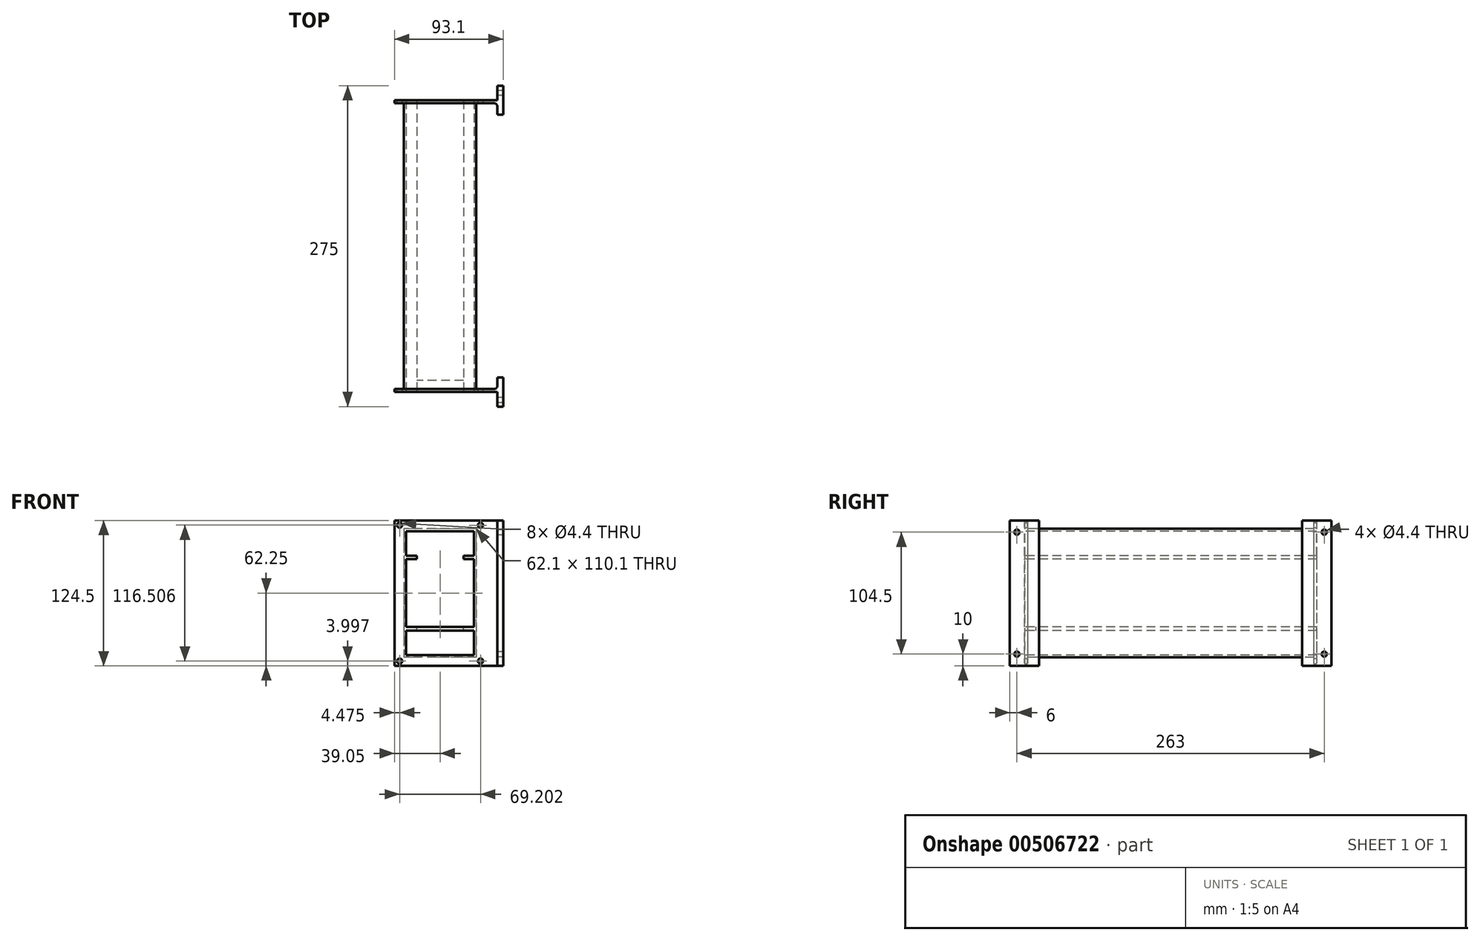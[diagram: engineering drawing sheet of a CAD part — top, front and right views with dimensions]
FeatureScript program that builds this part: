
annotation { "Feature Type Name" : "Feature", "Feature Type Description" : "" }
export const myFeature = defineFeature(function(context is Context, id is Id, definition is map)
    precondition{}
    {
        {
            var Q0;
            Q0=qCreatedBy(makeId("Front.planeOp"),FACE);
            var sketch = newSketch(context, id + "F0", { "sketchPlane" : qUnion([Q0])});
            skLineSegment(sketch, "E0.bottom", {"start": v(39.05, 62.25) * mm, "end": v(-39.05, 62.25) * mm});
            skLineSegment(sketch, "E0.top", {"start": v(39.05, -62.25) * mm, "end": v(-39.05, -62.25) * mm});
            skLineSegment(sketch, "E0.left", {"start": v(39.05, 62.25) * mm, "end": v(39.05, -62.25) * mm});
            skLineSegment(sketch, "E0.right", {"start": v(-39.05, 62.25) * mm, "end": v(-39.05, -62.25) * mm});
            skPoint(sketch, "E0.middle", {"position": v(0, 0) * mm});
            skLineSegment(sketch, "E1.bottom", {"start": v(29.05, 29.05) * mm, "end": v(-29.05, 29.05) * mm});
            skLineSegment(sketch, "E1.top", {"start": v(29.05, -29.05) * mm, "end": v(-29.05, -29.05) * mm});
            skLineSegment(sketch, "E1.left", {"start": v(29.05, 29.05) * mm, "end": v(29.05, -29.05) * mm});
            skLineSegment(sketch, "E1.right", {"start": v(-29.05, 29.05) * mm, "end": v(-29.05, -29.05) * mm});
            skLineSegment(sketch, "E2.bottom", {"start": v(-29.05, 29.05) * mm, "end": v(29.05, 29.05) * mm});
            skLineSegment(sketch, "E2.top", {"start": v(-29.05, 53.05) * mm, "end": v(29.05, 53.05) * mm});
            skLineSegment(sketch, "E2.left", {"start": v(-29.05, 29.05) * mm, "end": v(-29.05, 53.05) * mm});
            skLineSegment(sketch, "E2.right", {"start": v(29.05, 29.05) * mm, "end": v(29.05, 53.05) * mm});
            skLineSegment(sketch, "E3.bottom", {"start": v(-29.05, -29.05) * mm, "end": v(29.05, -29.05) * mm});
            skLineSegment(sketch, "E3.top", {"start": v(-29.05, -53.05) * mm, "end": v(29.05, -53.05) * mm});
            skLineSegment(sketch, "E3.left", {"start": v(-29.05, -29.05) * mm, "end": v(-29.05, -53.05) * mm});
            skLineSegment(sketch, "E3.right", {"start": v(29.05, -29.05) * mm, "end": v(29.05, -53.05) * mm});
            skLineSegment(sketch, "E4", {"start": v(0, 33.08) * mm, "end": v(0, 29.05) * mm, "construction": true});
            skLineSegment(sketch, "E5", {"start": v(29.05, 0) * mm, "end": v(-29.05, 0) * mm, "construction": true});
            skLineSegment(sketch, "E6.0", {"start": v(-29.05, 32.05) * mm, "end": v(29.05, 32.05) * mm});
            skLineSegment(sketch, "E7.0", {"start": v(-20, 33.08) * mm, "end": v(-20, 29.05) * mm, "construction": true});
            skLineSegment(sketch, "E8.0", {"start": v(20, 33.08) * mm, "end": v(20, 29.05) * mm, "construction": true});
            skLineSegment(sketch, "E9.bottom", {"start": v(20, 32.05) * mm, "end": v(-20, 32.05) * mm});
            skLineSegment(sketch, "E9.top", {"start": v(20, 29.05) * mm, "end": v(-20, 29.05) * mm});
            skLineSegment(sketch, "E9.left", {"start": v(20, 32.05) * mm, "end": v(20, 29.05) * mm});
            skLineSegment(sketch, "E9.right", {"start": v(-20, 32.05) * mm, "end": v(-20, 29.05) * mm});
            skLineSegment(sketch, "E10.MirrorCS", {"start": v(20, -32.05) * mm, "end": v(20, -29.05) * mm});
            skLineSegment(sketch, "E11.MirrorCS", {"start": v(-29.05, -32.05) * mm, "end": v(29.05, -32.05) * mm});
            skLineSegment(sketch, "E12.MirrorCS", {"start": v(-20, -32.05) * mm, "end": v(-20, -29.05) * mm});
            skLineSegment(sketch, "E13.bottom", {"start": v(39.05, 62.25) * mm, "end": v(49.05, 62.25) * mm});
            skLineSegment(sketch, "E13.top", {"start": v(39.05, -62.25) * mm, "end": v(49.05, -62.25) * mm});
            skLineSegment(sketch, "E13.right", {"start": v(49.05, 62.25) * mm, "end": v(49.05, -62.25) * mm});
            skLineSegment(sketch, "E14.bottom", {"start": v(49.05, 62.25) * mm, "end": v(54.05, 62.25) * mm});
            skLineSegment(sketch, "E14.top", {"start": v(49.05, -62.25) * mm, "end": v(54.05, -62.25) * mm});
            skLineSegment(sketch, "E14.right", {"start": v(54.05, 62.25) * mm, "end": v(54.05, -62.25) * mm});
            skSolve(sketch);
        }
        {
            var Q0;
            Q0=makeQuery(id+"F0.imprint","IMPRINT",FACE,{"disambiguationData":[TD([[makeQuery(id+"F0.imprint","IMPRINT",EDGE,{"derivedFrom":sQuery(id+"F0.wireOp",EDGE,"E0.bottom")}),1.0]])]});
            extrude(context, id + "F1", {"entities" : qUnion([Q0]), "oppositeDirection" : true, "depth" : 2.5 * mm, "offsetDistance" : 25 * mm});
        }
        {
            var Q0;
            {var subQ3=sQuery(id+"F0.wireOp",EDGE,"E9.left");Q0=makeQuery(id+"F0.imprint","IMPRINT",FACE,{"disambiguationData":[TD([[makeQuery(id+"F0.imprint","IMPRINT",EDGE,{"derivedFrom":subQ3}),1.0]])]});}
            var Q1;
            {var subQ3=sQuery(id+"F0.wireOp",EDGE,"E9.right");Q1=makeQuery(id+"F0.imprint","IMPRINT",FACE,{"disambiguationData":[TD([[makeQuery(id+"F0.imprint","IMPRINT",EDGE,{"derivedFrom":subQ3}),-1.0]])]});}
            var Q2;
            {var subQ3=sQuery(id+"F0.wireOp",EDGE,"E10.MirrorCS");Q2=makeQuery(id+"F0.imprint","IMPRINT",FACE,{"disambiguationData":[TD([[makeQuery(id+"F0.imprint","IMPRINT",EDGE,{"derivedFrom":subQ3}),-1.0]])]});}
            var Q3;
            {var subQ3=sQuery(id+"F0.wireOp",EDGE,"E12.MirrorCS");Q3=makeQuery(id+"F0.imprint","IMPRINT",FACE,{"disambiguationData":[TD([[makeQuery(id+"F0.imprint","IMPRINT",EDGE,{"derivedFrom":subQ3}),1.0]])]});}
            extrude(context, id + "F2", {"entities" : qUnion([Q0, Q1, Q2, Q3]), "operationType" : NewBodyOperationType.ADD, "oppositeDirection" : true, "depth" : 250 * mm, "offsetDistance" : 25 * mm});
        }
        {
            var Q0;
            Q0=makeQuery(id+"F0.imprint","IMPRINT",FACE,{"disambiguationData":[TD([[makeQuery(id+"F0.imprint","IMPRINT",EDGE,{"derivedFrom":sQuery(id+"F0.wireOp",EDGE,"E9.bottom")}),1.0]])]});
            var Q1;
            {var subQ0=sQuery(id+"F0.wireOp",EDGE,"E10.MirrorCS");Q1=makeQuery(id+"F0.imprint","IMPRINT",FACE,{"disambiguationData":[TD([[makeQuery(id+"F0.imprint","IMPRINT",EDGE,{"derivedFrom":subQ0}),1.0]])]});}
            extrude(context, id + "F3", {"entities" : qUnion([Q0, Q1]), "operationType" : NewBodyOperationType.ADD, "oppositeDirection" : true, "depth" : 10 * mm, "offsetDistance" : 25 * mm});
        }
        {
            var Q0;
            Q0=makeQuery(id+"F1.opExtrude","CAP_FACE",FACE,{"disambiguationData":[OSD([sQuery(id+"F0.wireOp",EDGE,"E0.bottom"),sQuery(id+"F0.wireOp",EDGE,"E0.top"),sQuery(id+"F0.wireOp",EDGE,"E0.left"),sQuery(id+"F0.wireOp",EDGE,"E0.right"),sQuery(id+"F0.wireOp",EDGE,"E1.left"),sQuery(id+"F0.wireOp",EDGE,"E1.right"),sQuery(id+"F0.wireOp",EDGE,"E2.top"),sQuery(id+"F0.wireOp",EDGE,"E2.left"),sQuery(id+"F0.wireOp",EDGE,"E2.right"),sQuery(id+"F0.wireOp",EDGE,"E3.top"),sQuery(id+"F0.wireOp",EDGE,"E3.left"),sQuery(id+"F0.wireOp",EDGE,"E3.right"),sQuery(id+"F0.wireOp",EDGE,"4e601988-f2da-406f-8835-c61af852b349.0"),sQuery(id+"F0.wireOp",EDGE,"4e601988-f2da-406f-8835-c61af852b349.1"),sQuery(id+"F0.wireOp",EDGE,"4e601988-f2da-406f-8835-c61af852b349.2"),sQuery(id+"F0.wireOp",EDGE,"4e601988-f2da-406f-8835-c61af852b349.3")])],"isStart":false});
            cPlane(context, id + "F4", {"entities" : qUnion([Q0]), "cplaneType" : CPlaneType.OFFSET, "offset" : 0 * mm, "width" : 150 * mm, "height" : 150 * mm});
        }
        {
            var Q0;
            Q0=qCreatedBy(id+"F4.planeOp",FACE);
            var sketch = newSketch(context, id + "F5", { "sketchPlane" : qUnion([Q0])});
            skLineSegment(sketch, "E15.0", {"start": v(-29.05, -29.05) * mm, "end": v(-29.05, -53.05) * mm});
            skLineSegment(sketch, "E16.0", {"start": v(29.05, -29.05) * mm, "end": v(29.05, -53.05) * mm});
            skLineSegment(sketch, "E17.0", {"start": v(-29.05, 29.05) * mm, "end": v(-29.05, 53.05) * mm});
            skLineSegment(sketch, "E17.1", {"start": v(29.05, 29.05) * mm, "end": v(29.05, 53.05) * mm});
            skLineSegment(sketch, "E18.bottom", {"start": v(-29.05, 53.05) * mm, "end": v(29.05, 53.05) * mm});
            skLineSegment(sketch, "E18.top", {"start": v(-29.05, -53.05) * mm, "end": v(29.05, -53.05) * mm});
            skLineSegment(sketch, "E18.left", {"start": v(-29.05, 53.05) * mm, "end": v(-29.05, -53.05) * mm});
            skLineSegment(sketch, "E18.right", {"start": v(29.05, 53.05) * mm, "end": v(29.05, -53.05) * mm});
            skLineSegment(sketch, "E19.0", {"start": v(-31.05, 55.05) * mm, "end": v(31.05, 55.05) * mm});
            skLineSegment(sketch, "E19.1", {"start": v(-31.05, 55.05) * mm, "end": v(-31.05, -55.05) * mm});
            skLineSegment(sketch, "E19.2", {"start": v(-31.05, -55.05) * mm, "end": v(31.05, -55.05) * mm});
            skLineSegment(sketch, "E19.3", {"start": v(31.05, 55.05) * mm, "end": v(31.05, -55.05) * mm});
            skSolve(sketch);
        }
        {
            var Q0;
            {var subQ4=sQuery(id+"F5.wireOp",EDGE,"E18.bottom");Q0=makeQuery(id+"F5.imprint","IMPRINT",FACE,{"disambiguationData":[TD([[makeQuery(id+"F5.imprint","IMPRINT",EDGE,{"derivedFrom":subQ4}),1.0]])]});}
            extrude(context, id + "F6", {"entities" : qUnion([Q0]), "operationType" : NewBodyOperationType.ADD, "depth" : 247.5 * mm, "offsetDistance" : 25 * mm});
        }
        {
            var Q0;
            {var subQ0=sQuery(id+"F0.wireOp",EDGE,"E11.MirrorCS");var subQ1=sQuery(id+"F0.wireOp",EDGE,"E3.bottom");var subQ2=sQuery(id+"F0.wireOp",EDGE,"E6.0");var subQ3=sQuery(id+"F0.wireOp",EDGE,"E2.bottom");Q0=makeQuery(id+"F6.boolean.opBoolean","MERGE",FACE,{"derivedFrom":[makeQuery(id+"F2.opExtrude","CAP_FACE",FACE,{"disambiguationData":[OSD([subQ3,sQuery(id+"F0.wireOp",EDGE,"E2.left"),subQ2,sQuery(id+"F0.wireOp",EDGE,"E9.right")])],"isStart":false}),makeQuery(id+"F2.opExtrude","CAP_FACE",FACE,{"disambiguationData":[OSD([subQ3,sQuery(id+"F0.wireOp",EDGE,"E2.right"),subQ2,sQuery(id+"F0.wireOp",EDGE,"E9.left")])],"isStart":false}),makeQuery(id+"F2.opExtrude","CAP_FACE",FACE,{"disambiguationData":[OSD([subQ1,sQuery(id+"F0.wireOp",EDGE,"E3.left"),subQ0,sQuery(id+"F0.wireOp",EDGE,"E12.MirrorCS")])],"isStart":false}),makeQuery(id+"F2.opExtrude","CAP_FACE",FACE,{"disambiguationData":[OSD([subQ1,sQuery(id+"F0.wireOp",EDGE,"E3.right"),sQuery(id+"F0.wireOp",EDGE,"E10.MirrorCS"),subQ0])],"isStart":false}),makeQuery(id+"F6.opExtrude","CAP_FACE",FACE,{"disambiguationData":[OSD([sQuery(id+"F5.wireOp",EDGE,"E18.bottom"),sQuery(id+"F5.wireOp",EDGE,"E18.top"),sQuery(id+"F5.wireOp",EDGE,"E18.left"),sQuery(id+"F5.wireOp",EDGE,"E18.right"),sQuery(id+"F5.wireOp",EDGE,"E19.0"),sQuery(id+"F5.wireOp",EDGE,"E19.1"),sQuery(id+"F5.wireOp",EDGE,"E19.2"),sQuery(id+"F5.wireOp",EDGE,"E19.3")])],"isStart":false})]});}
            cPlane(context, id + "F7", {"entities" : qUnion([Q0]), "cplaneType" : CPlaneType.OFFSET, "offset" : 0 * mm, "width" : 150 * mm, "height" : 150 * mm});
        }
        {
            var Q0;
            Q0=qCreatedBy(id+"F7.planeOp",FACE);
            var sketch = newSketch(context, id + "F8", { "sketchPlane" : qUnion([Q0])});
            skLineSegment(sketch, "E20.2", {"start": v(39.05, 62.25) * mm, "end": v(39.05, -62.25) * mm});
            skLineSegment(sketch, "E20.4", {"start": v(-31.05, -55.05) * mm, "end": v(31.05, -55.05) * mm});
            skLineSegment(sketch, "E20.5", {"start": v(31.05, 55.05) * mm, "end": v(31.05, -55.05) * mm});
            skLineSegment(sketch, "E20.6", {"start": v(-31.05, 55.05) * mm, "end": v(-31.05, -55.05) * mm});
            skLineSegment(sketch, "E20.7", {"start": v(-31.05, 55.05) * mm, "end": v(31.05, 55.05) * mm});
            skLineSegment(sketch, "E20.8", {"start": v(-20, 32.05) * mm, "end": v(-29.05, 32.05) * mm});
            skLineSegment(sketch, "E20.9", {"start": v(-20, 32.05) * mm, "end": v(-20, 29.05) * mm});
            skLineSegment(sketch, "E20.10", {"start": v(-20, 29.05) * mm, "end": v(-29.05, 29.05) * mm});
            skLineSegment(sketch, "E20.11", {"start": v(-20, 32.05) * mm, "end": v(20, 32.05) * mm});
            skLineSegment(sketch, "E20.12", {"start": v(-20, 29.05) * mm, "end": v(20, 29.05) * mm});
            skLineSegment(sketch, "E20.13", {"start": v(-29.05, 29.05) * mm, "end": v(-29.05, -29.05) * mm});
            skLineSegment(sketch, "E20.14", {"start": v(20, 32.05) * mm, "end": v(20, 29.05) * mm});
            skLineSegment(sketch, "E20.15", {"start": v(29.05, 32.05) * mm, "end": v(20, 32.05) * mm});
            skLineSegment(sketch, "E20.16", {"start": v(29.05, 29.05) * mm, "end": v(20, 29.05) * mm});
            skLineSegment(sketch, "E20.17", {"start": v(29.05, 29.05) * mm, "end": v(29.05, -29.05) * mm});
            skLineSegment(sketch, "E20.18", {"start": v(-20, -29.05) * mm, "end": v(-29.05, -29.05) * mm});
            skLineSegment(sketch, "E20.19", {"start": v(20, -32.05) * mm, "end": v(-20, -32.05) * mm});
            skLineSegment(sketch, "E20.20", {"start": v(20, -29.05) * mm, "end": v(-20, -29.05) * mm});
            skLineSegment(sketch, "E20.21", {"start": v(-20, -32.05) * mm, "end": v(-29.05, -32.05) * mm});
            skLineSegment(sketch, "E20.22", {"start": v(-20, -32.05) * mm, "end": v(-20, -29.05) * mm});
            skLineSegment(sketch, "E20.23", {"start": v(20, -32.05) * mm, "end": v(20, -29.05) * mm});
            skLineSegment(sketch, "E20.24", {"start": v(29.05, -32.05) * mm, "end": v(20, -32.05) * mm});
            skLineSegment(sketch, "E20.25", {"start": v(29.05, -29.05) * mm, "end": v(20, -29.05) * mm});
            skLineSegment(sketch, "E20.26", {"start": v(-29.05, -32.05) * mm, "end": v(-29.05, -53.05) * mm});
            skLineSegment(sketch, "E20.27", {"start": v(-29.05, -53.05) * mm, "end": v(29.05, -53.05) * mm});
            skLineSegment(sketch, "E20.28", {"start": v(29.05, -32.05) * mm, "end": v(29.05, -53.05) * mm});
            skLineSegment(sketch, "E20.29", {"start": v(-29.05, 53.05) * mm, "end": v(-29.05, 32.05) * mm});
            skLineSegment(sketch, "E20.30", {"start": v(-29.05, 53.05) * mm, "end": v(29.05, 53.05) * mm});
            skLineSegment(sketch, "E20.31", {"start": v(29.05, 53.05) * mm, "end": v(29.05, 32.05) * mm});
            skLineSegment(sketch, "E21.0", {"start": v(-49.05, 62.25) * mm, "end": v(-49.05, -62.25) * mm});
            skLineSegment(sketch, "E22.bottom", {"start": v(-49.05, 62.25) * mm, "end": v(39.05, 62.25) * mm});
            skLineSegment(sketch, "E22.top", {"start": v(-49.05, -62.25) * mm, "end": v(39.05, -62.25) * mm});
            skLineSegment(sketch, "E23.0", {"start": v(-39.05, 62.25) * mm, "end": v(-39.05, -62.25) * mm});
            skLineSegment(sketch, "E24", {"start": v(-39.05, -62.25) * mm, "end": v(-34.63, -58.2) * mm, "construction": true});
            skLineSegment(sketch, "E25", {"start": v(39.05, -62.25) * mm, "end": v(34.58, -58.25) * mm, "construction": true});
            skLineSegment(sketch, "E26.MirrorCS", {"start": v(-39.05, 62.25) * mm, "end": v(-34.63, 58.2) * mm, "construction": true});
            skLineSegment(sketch, "E27.MirrorCS", {"start": v(39.05, 62.25) * mm, "end": v(34.58, 58.25) * mm, "construction": true});
            skLineSegment(sketch, "E28.0.0", {"start": v(-54.05, 62.25) * mm, "end": v(-49.05, 62.25) * mm});
            skLineSegment(sketch, "E28.0.2", {"start": v(-49.05, -62.25) * mm, "end": v(-54.05, -62.25) * mm});
            skLineSegment(sketch, "E28.0.3", {"start": v(-54.05, -62.25) * mm, "end": v(-54.05, 62.25) * mm});
            skSolve(sketch);
        }
        {
            var Q0;
            Q0=makeQuery(id+"F8.imprint","IMPRINT",FACE,{"disambiguationData":[TD([[makeQuery(id+"F8.imprint","IMPRINT",EDGE,{"derivedFrom":sQuery(id+"F8.wireOp",EDGE,"E20.4")}),-1.0]])]});
            extrude(context, id + "F9", {"entities" : qUnion([Q0]), "operationType" : NewBodyOperationType.ADD, "oppositeDirection" : true, "depth" : 2.5 * mm, "offsetDistance" : 25 * mm});
        }
        {
            var Q0;
            Q0=makeQuery(id+"F8.imprint","IMPRINT",FACE,{"disambiguationData":[TD([[makeQuery(id+"F8.imprint","IMPRINT",EDGE,{"derivedFrom":sQuery(id+"F8.wireOp",EDGE,"E28.0.0")}),-1.0]])]});
            extrude(context, id + "F10", {"entities" : qUnion([Q0]), "operationType" : NewBodyOperationType.ADD, "depth" : 12.5 * mm, "offsetDistance" : 25 * mm, "hasSecondDirection" : true, "secondDirectionOppositeDirection" : true, "secondDirectionDepth" : 12.5 * mm});
        }
        {
            var Q0;
            Q0=makeQuery(id+"F0.imprint","IMPRINT",FACE,{"disambiguationData":[TD([[makeQuery(id+"F0.imprint","IMPRINT",EDGE,{"derivedFrom":sQuery(id+"F0.wireOp",EDGE,"E14.bottom")}),-1.0]])]});
            extrude(context, id + "F11", {"entities" : qUnion([Q0]), "operationType" : NewBodyOperationType.ADD, "depth" : 12.5 * mm, "offsetDistance" : 25 * mm, "hasSecondDirection" : true, "secondDirectionOppositeDirection" : true, "secondDirectionDepth" : 12.5 * mm});
        }
        {
            var Q0;
            Q0=makeQuery(id+"F11.opExtrude","SWEPT_FACE",FACE,{"disambiguationData":[OSD([sQuery(id+"F0.wireOp",EDGE,"E14.right")])]});
            cPlane(context, id + "F12", {"entities" : qUnion([Q0]), "cplaneType" : CPlaneType.OFFSET, "offset" : 0 * mm, "width" : 150 * mm, "height" : 150 * mm});
        }
        {
            var Q0;
            Q0=qCreatedBy(id+"F12.planeOp",FACE);
            var sketch = newSketch(context, id + "F13", { "sketchPlane" : qUnion([Q0])});
            skLineSegment(sketch, "E29.0.0", {"start": v(12.5, -62.25) * mm, "end": v(12.5, 62.25) * mm});
            skLineSegment(sketch, "E29.0.1", {"start": v(12.5, 62.25) * mm, "end": v(-12.5, 62.25) * mm});
            skLineSegment(sketch, "E29.0.2", {"start": v(-12.5, 62.25) * mm, "end": v(-12.5, -62.25) * mm});
            skLineSegment(sketch, "E29.0.3", {"start": v(-12.5, -62.25) * mm, "end": v(12.5, -62.25) * mm});
            skLineSegment(sketch, "E30", {"start": v(-12.5, 62.25) * mm, "end": v(-6.5, 62.25) * mm, "construction": true});
            skLineSegment(sketch, "E31", {"start": v(-6.5, 62.25) * mm, "end": v(-6.5, 52.25) * mm, "construction": true});
            skLineSegment(sketch, "E32", {"start": v(-12.5, 0) * mm, "end": v(0, 0) * mm, "construction": true});
            skLineSegment(sketch, "E33.MirrorCS", {"start": v(-6.5, -62.25) * mm, "end": v(-6.5, -52.25) * mm, "construction": true});
            skLineSegment(sketch, "E34.MirrorCS", {"start": v(-12.5, -62.25) * mm, "end": v(-6.5, -62.25) * mm, "construction": true});
            skLineSegment(sketch, "E35", {"start": v(-12.5, 0) * mm, "end": v(-8.96, 0) * mm, "construction": true});
            skSolve(sketch);
        }
        {
            var Q0;
            Q0=makeQuery(id+"F10.opExtrude","SWEPT_FACE",FACE,{"disambiguationData":[OSD([sQuery(id+"F8.wireOp",EDGE,"E28.0.3")])]});
            cPlane(context, id + "F14", {"entities" : qUnion([Q0]), "cplaneType" : CPlaneType.OFFSET, "offset" : 0 * mm, "width" : 150 * mm, "height" : 150 * mm});
        }
        {
            var Q0;
            Q0=qCreatedBy(id+"F14.planeOp",FACE);
            var sketch = newSketch(context, id + "F15", { "sketchPlane" : qUnion([Q0])});
            skLineSegment(sketch, "E36.0.0", {"start": v(237.5, 62.25) * mm, "end": v(237.5, -62.25) * mm});
            skLineSegment(sketch, "E36.0.1", {"start": v(237.5, -62.25) * mm, "end": v(262.5, -62.25) * mm});
            skLineSegment(sketch, "E36.0.2", {"start": v(262.5, -62.25) * mm, "end": v(262.5, 62.25) * mm});
            skLineSegment(sketch, "E36.0.3", {"start": v(262.5, 62.25) * mm, "end": v(237.5, 62.25) * mm});
            skLineSegment(sketch, "E37", {"start": v(262.5, 62.25) * mm, "end": v(256.5, 62.25) * mm, "construction": true});
            skLineSegment(sketch, "E38", {"start": v(256.5, 62.25) * mm, "end": v(256.5, 52.25) * mm, "construction": true});
            skLineSegment(sketch, "E39", {"start": v(262.5, 0) * mm, "end": v(237.5, 0) * mm, "construction": true});
            skLineSegment(sketch, "E40.MirrorCS", {"start": v(262.5, -62.25) * mm, "end": v(256.5, -62.25) * mm, "construction": true});
            skLineSegment(sketch, "E41.MirrorCS", {"start": v(262.5, 62.25) * mm, "end": v(262.5, -62.25) * mm});
            skLineSegment(sketch, "E42.MirrorCS", {"start": v(262.5, -62.25) * mm, "end": v(237.5, -62.25) * mm});
            skLineSegment(sketch, "E43.MirrorCS", {"start": v(256.5, -62.25) * mm, "end": v(256.5, -52.25) * mm, "construction": true});
            skSolve(sketch);
        }
        {
            var Q0;
            Q0=sQuery(id+"F8.wireOp",VERTEX,"E26.MirrorCS.end");
            var Q1;
            Q1=sQuery(id+"F8.wireOp",VERTEX,"E27.MirrorCS.end");
            var Q2;
            Q2=sQuery(id+"F8.wireOp",VERTEX,"E24.end");
            var Q3;
            Q3=sQuery(id+"F8.wireOp",VERTEX,"E25.end");
            var Q4;
            Q4=makeQuery(id+"F1.opExtrude","SWEPT_BODY",BODY,{"disambiguationData":[OSD([sQuery(id+"F0.wireOp",EDGE,"E0.bottom"),sQuery(id+"F0.wireOp",EDGE,"E0.top"),sQuery(id+"F0.wireOp",EDGE,"E0.right"),sQuery(id+"F0.wireOp",EDGE,"E1.left"),sQuery(id+"F0.wireOp",EDGE,"E1.right"),sQuery(id+"F0.wireOp",EDGE,"E2.top"),sQuery(id+"F0.wireOp",EDGE,"E2.left"),sQuery(id+"F0.wireOp",EDGE,"E2.right"),sQuery(id+"F0.wireOp",EDGE,"E3.top"),sQuery(id+"F0.wireOp",EDGE,"E3.left"),sQuery(id+"F0.wireOp",EDGE,"E3.right"),sQuery(id+"F0.wireOp",EDGE,"4e601988-f2da-406f-8835-c61af852b349.0"),sQuery(id+"F0.wireOp",EDGE,"4e601988-f2da-406f-8835-c61af852b349.1"),sQuery(id+"F0.wireOp",EDGE,"4e601988-f2da-406f-8835-c61af852b349.2"),sQuery(id+"F0.wireOp",EDGE,"4e601988-f2da-406f-8835-c61af852b349.3"),sQuery(id+"F0.wireOp",EDGE,"E0.left")])]});
            hole(context, id + "F16", {"style" : HoleStyle.SIMPLE, "endStyle" : HoleEndStyle.THROUGH, "standardTappedOrClearance" : lookupTablePath({ "standard" : "ISO", "fit" : "Normal", "size" : "M4", "type" : "Clearance" }), "standardBlindInLast" : lookupTablePath({ "fit" : "Standard", "standard" : "ISO", "size" : "M4", "type" : "Clearance" }), "holeDiameter" : 4.4 * mm, "majorDiameter" : 5 * mm, "isTappedThrough" : true, "tappedDepth" : 12 * mm, "tapClearance" : 3, "locations" : qUnion([Q0, Q1, Q2, Q3]), "scope" : qUnion([Q4])});
        }
        {
            var Q0;
            Q0=makeQuery(id+"F0.imprint","IMPRINT",FACE,{"disambiguationData":[TD([[makeQuery(id+"F0.imprint","IMPRINT",EDGE,{"derivedFrom":sQuery(id+"F0.wireOp",EDGE,"E13.bottom")}),-1.0]])]});
            extrude(context, id + "F17", {"entities" : qUnion([Q0]), "operationType" : NewBodyOperationType.ADD, "oppositeDirection" : true, "depth" : 2.5 * mm, "offsetDistance" : 25 * mm});
        }
        {
            var Q0;
            Q0=makeQuery(id+"F17.opExtrude","CAP_EDGE",EDGE,{"disambiguationData":[OSD([sQuery(id+"F0.wireOp",EDGE,"E13.right")])],"isStart":false});
            var Q1;
            Q1=makeQuery(id+"F6.opExtrude","CAP_EDGE",EDGE,{"disambiguationData":[OSD([sQuery(id+"F5.wireOp",EDGE,"E19.0")])],"isStart":true});
            var Q2;
            Q2=makeQuery(id+"F6.opExtrude","CAP_EDGE",EDGE,{"disambiguationData":[OSD([sQuery(id+"F5.wireOp",EDGE,"E19.1")])],"isStart":true});
            var Q3;
            Q3=makeQuery(id+"F17.opExtrude","CAP_EDGE",EDGE,{"disambiguationData":[OSD([sQuery(id+"F0.wireOp",EDGE,"E13.right")])],"isStart":true});
            var Q4;
            Q4=makeQuery(id+"F6.opExtrude","CAP_EDGE",EDGE,{"disambiguationData":[OSD([sQuery(id+"F5.wireOp",EDGE,"E19.3")])],"isStart":true});
            var Q5;
            Q5=makeQuery(id+"F6.opExtrude","CAP_EDGE",EDGE,{"disambiguationData":[OSD([sQuery(id+"F5.wireOp",EDGE,"E19.2")])],"isStart":true});
            fillet(context, id + "F18", {"entities" : qUnion([Q0, Q1, Q2, Q3, Q4, Q5]), "radius" : 3 * mm, "tangentPropagation" : true, "allowEdgeOverflow" : false});
        }
        {
            var Q0;
            Q0=sQuery(id+"F13.wireOp",VERTEX,"E33.MirrorCS.end");
            var Q1;
            Q1=sQuery(id+"F13.wireOp",VERTEX,"E31.end");
            var Q2;
            Q2=makeQuery(id+"F1.opExtrude","SWEPT_BODY",BODY,{"disambiguationData":[OSD([sQuery(id+"F0.wireOp",EDGE,"E0.bottom"),sQuery(id+"F0.wireOp",EDGE,"E0.top"),sQuery(id+"F0.wireOp",EDGE,"E0.right"),sQuery(id+"F0.wireOp",EDGE,"E1.left"),sQuery(id+"F0.wireOp",EDGE,"E1.right"),sQuery(id+"F0.wireOp",EDGE,"E2.top"),sQuery(id+"F0.wireOp",EDGE,"E2.left"),sQuery(id+"F0.wireOp",EDGE,"E2.right"),sQuery(id+"F0.wireOp",EDGE,"E3.top"),sQuery(id+"F0.wireOp",EDGE,"E3.left"),sQuery(id+"F0.wireOp",EDGE,"E3.right"),sQuery(id+"F0.wireOp",EDGE,"E0.left")])]});
            hole(context, id + "F19", {"style" : HoleStyle.SIMPLE, "endStyle" : HoleEndStyle.THROUGH, "standardTappedOrClearance" : lookupTablePath({ "standard" : "ISO", "fit" : "Normal", "size" : "M4", "type" : "Clearance" }), "standardBlindInLast" : lookupTablePath({ "fit" : "Standard", "standard" : "ISO", "size" : "M4", "type" : "Clearance" }), "holeDiameter" : 4.4 * mm, "majorDiameter" : 5 * mm, "isTappedThrough" : true, "tappedDepth" : 12 * mm, "tapClearance" : 3, "locations" : qUnion([Q0, Q1]), "scope" : qUnion([Q2])});
        }
        {
            var Q0;
            {var subQ2=sQuery(id+"F8.wireOp",EDGE,"E23.0");Q0=makeQuery(id+"F8.imprint","IMPRINT",FACE,{"disambiguationData":[TD([[makeQuery(id+"F8.imprint","IMPRINT",EDGE,{"derivedFrom":subQ2}),-1.0]])]});}
            extrude(context, id + "F20", {"entities" : qUnion([Q0]), "operationType" : NewBodyOperationType.ADD, "oppositeDirection" : true, "depth" : 2.5 * mm, "offsetDistance" : 25 * mm});
        }
        {
            var Q0;
            Q0=makeQuery(id+"F20.opExtrude","CAP_EDGE",EDGE,{"disambiguationData":[OSD([sQuery(id+"F8.wireOp",EDGE,"E21.0")])],"isStart":true});
            var Q1;
            Q1=makeQuery(id+"F9.opExtrude","CAP_EDGE",EDGE,{"disambiguationData":[OSD([sQuery(id+"F8.wireOp",EDGE,"E20.4")])],"isStart":false});
            var Q2;
            Q2=makeQuery(id+"F20.opExtrude","CAP_EDGE",EDGE,{"disambiguationData":[OSD([sQuery(id+"F8.wireOp",EDGE,"E21.0")])],"isStart":false});
            var Q3;
            Q3=makeQuery(id+"F9.opExtrude","CAP_EDGE",EDGE,{"disambiguationData":[OSD([sQuery(id+"F8.wireOp",EDGE,"E20.5")])],"isStart":false});
            var Q4;
            Q4=makeQuery(id+"F9.opExtrude","CAP_EDGE",EDGE,{"disambiguationData":[OSD([sQuery(id+"F8.wireOp",EDGE,"E20.6")])],"isStart":false});
            var Q5;
            Q5=makeQuery(id+"F9.opExtrude","CAP_EDGE",EDGE,{"disambiguationData":[OSD([sQuery(id+"F8.wireOp",EDGE,"E20.7")])],"isStart":false});
            fillet(context, id + "F21", {"entities" : qUnion([Q0, Q1, Q2, Q3, Q4, Q5]), "radius" : 3 * mm, "tangentPropagation" : true, "allowEdgeOverflow" : false});
        }
        {
            var Q0;
            Q0=sQuery(id+"F15.wireOp",VERTEX,"E38.end");
            var Q1;
            Q1=sQuery(id+"F15.wireOp",VERTEX,"E43.MirrorCS.end");
            var Q2;
            Q2=sQuery(id+"F13.wireOp",VERTEX,"E33.MirrorCS.end");
            var Q3;
            Q3=sQuery(id+"F13.wireOp",VERTEX,"jfUWSlUZ-1aHR-QNzQ-WiYN-HiqFYwwCv3jF.center");
            var Q4;
            Q4=makeQuery(id+"F1.opExtrude","SWEPT_BODY",BODY,{"disambiguationData":[OSD([sQuery(id+"F0.wireOp",EDGE,"E0.bottom"),sQuery(id+"F0.wireOp",EDGE,"E0.top"),sQuery(id+"F0.wireOp",EDGE,"E0.right"),sQuery(id+"F0.wireOp",EDGE,"E1.left"),sQuery(id+"F0.wireOp",EDGE,"E1.right"),sQuery(id+"F0.wireOp",EDGE,"E2.top"),sQuery(id+"F0.wireOp",EDGE,"E2.left"),sQuery(id+"F0.wireOp",EDGE,"E2.right"),sQuery(id+"F0.wireOp",EDGE,"E3.top"),sQuery(id+"F0.wireOp",EDGE,"E3.left"),sQuery(id+"F0.wireOp",EDGE,"E3.right"),sQuery(id+"F0.wireOp",EDGE,"4e601988-f2da-406f-8835-c61af852b349.0"),sQuery(id+"F0.wireOp",EDGE,"4e601988-f2da-406f-8835-c61af852b349.1"),sQuery(id+"F0.wireOp",EDGE,"4e601988-f2da-406f-8835-c61af852b349.2"),sQuery(id+"F0.wireOp",EDGE,"4e601988-f2da-406f-8835-c61af852b349.3"),sQuery(id+"F0.wireOp",EDGE,"E0.left")])]});
            hole(context, id + "F22", {"style" : HoleStyle.SIMPLE, "endStyle" : HoleEndStyle.THROUGH, "standardTappedOrClearance" : lookupTablePath({ "standard" : "ISO", "fit" : "Normal", "size" : "M4", "type" : "Clearance" }), "standardBlindInLast" : lookupTablePath({ "fit" : "Standard", "standard" : "ISO", "size" : "M4", "type" : "Clearance" }), "holeDiameter" : 4.4 * mm, "majorDiameter" : 5 * mm, "isTappedThrough" : true, "tappedDepth" : 12 * mm, "tapClearance" : 3, "locations" : qUnion([Q0, Q1, Q2, Q3]), "scope" : qUnion([Q4])});
        }
    });
